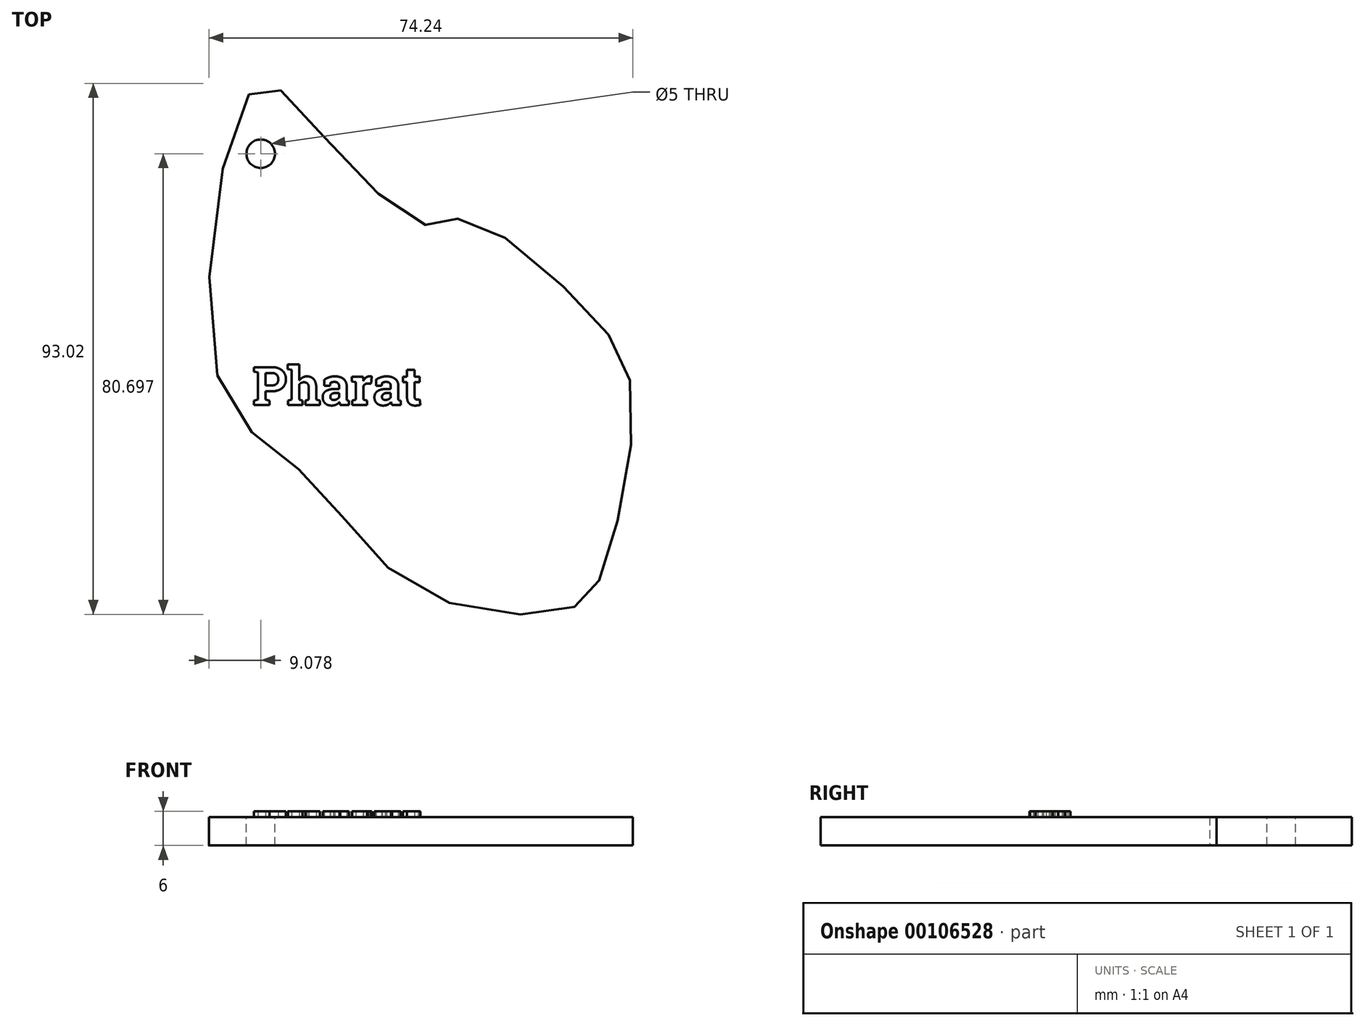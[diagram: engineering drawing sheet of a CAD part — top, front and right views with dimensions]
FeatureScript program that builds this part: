
annotation { "Feature Type Name" : "Feature", "Feature Type Description" : "" }
export const myFeature = defineFeature(function(context is Context, id is Id, definition is map)
    precondition{}
    {
        {
            var Q0;
            Q0=qCreatedBy(makeId("Top.planeOp"),FACE);
            var sketch = newSketch(context, id + "F0", { "sketchPlane" : qUnion([Q0])});
            skFitSpline(sketch, "E0", {"points": [v(0, 0) * mm, v(6.5, 50.33) * mm, v(15.34, 45.48) * mm, v(36.36, 26.32) * mm, v(43.19, 27.42) * mm, v(65.15, 10.95) * mm, v(72.7, -4.6) * mm, v(67.34, -34.72) * mm, v(61.37, -41.01) * mm, v(35.23, -37.62) * mm, v(15.55, -17.7) * mm, v(0, 0) * mm]});
            skSolve(sketch);
        }
        {
            var Q0;
            Q0=makeQuery(id+"F0.imprint","IMPRINT",FACE,{"disambiguationData":[TD([[makeQuery(id+"F0.imprint","IMPRINT",EDGE,{"derivedFrom":sQuery(id+"F0.wireOp",EDGE,"E0")}),-1.0]])]});
            extrude(context, id + "F1", {"entities" : qUnion([Q0]), "depth" : 5 * mm});
        }
        {
            var Q0;
            Q0=makeQuery(id+"F1.opExtrude","CAP_FACE",FACE,{"disambiguationData":[OSD([sQuery(id+"F0.wireOp",EDGE,"E0")])],"isStart":false});
            var sketch = newSketch(context, id + "F2", { "sketchPlane" : qUnion([Q0])});
            skCircle(sketch, "E1", {"center": v(7.58, 38.8) * mm, "radius": 2.5 * mm});
            skSolve(sketch);
        }
        {
            var Q0;
            Q0=makeQuery(id+"F2.imprint","IMPRINT",FACE,{"disambiguationData":[TD([[makeQuery(id+"F2.imprint","IMPRINT",EDGE,{"derivedFrom":sQuery(id+"F2.wireOp",EDGE,"E1")}),1.0]])]});
            extrude(context, id + "F3", {"entities" : qUnion([Q0]), "operationType" : NewBodyOperationType.REMOVE, "endBound" : BoundingType.THROUGH_ALL, "oppositeDirection" : true, "depth" : 25 * mm});
        }
        {
            var Q0;
            Q0=makeQuery(id+"F1.opExtrude","CAP_FACE",FACE,{"disambiguationData":[OSD([sQuery(id+"F0.wireOp",EDGE,"E0")])],"isStart":false});
            var sketch = newSketch(context, id + "F4", { "sketchPlane" : qUnion([Q0])});
            skText(sketch, "E2", { "text": "Pharat", "fontName": "RobotoSlab-Bold.ttf"});
            const initialGuessF4  = {"E2": [0.00612, -0.00523, 1, 0, 0.00672]};
            skSetInitialGuess(sketch, initialGuessF4);
            skSolve(sketch);
        }
        {
            var Q0;
            Q0 = qSketchRegion(id + "F4", true);
            extrude(context, id + "F5", {"entities" : qUnion([Q0]), "operationType" : NewBodyOperationType.ADD, "depth" : 1 * mm});
        }
    });
